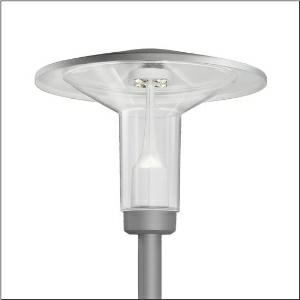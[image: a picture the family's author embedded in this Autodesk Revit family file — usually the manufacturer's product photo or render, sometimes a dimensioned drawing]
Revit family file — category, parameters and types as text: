
# Revit family: laterne_iq___pl1_2s_5xa5255jf14h_d587
name_source: partatom
category: Lighting Fixtures
units: mm (PartAtom-declared; Revit-internal decimal feet)

## family parameters
Cut with Voids When Loaded = No
Host = Face
Light Source = No
Part Type = Normal
Room Calculation Point = No
Round Connector Dimension = Use Diameter
Shared = No

## types (1)
- --- (1 x LED, 2970 lm, 19.3 W, 3000K)
    Apparent Load = 19 VA
    CIE Flux Codes = 25 63 94 98 100
    Color Rendering = 70
    Color Temperature = 3000K
    Default Elevation = 1800 mm
    Description = Lantern iQ, mast luminaire, Module 540 iQ-SR, primary light control with 3 zone facetted reflector, of plastic, silver coated, highly specular, structured, primary optical cover: cover, of PMMA, transparent, light distribution: PL1.2s, light emission: direct distribution, primary light characteristic: symmetric, installation type: post-top, LED, High Power LED, rated luminous flux: 2.970lm, luminous efficacy: 154lm/W, light colour: 730, colour temperature: 3000K, control gear: iQ Street-Remote, control: Auto-Match, Temp-Guard, Lumen-Switch, Night-Set, Smart-Wire, Light-Fading, Desk-Remote (wireless, voltage-free reading and setting of iQ features in the workshop via application-optimized NFC function/RFID function), optimised constant luminous flux control (CLO 2.0), Street-Remote, pre-setting: logarithmic dimming characteristic, with terminal, 6-pole, max. 2.5mm², mains connection: 230..240V, AC, 50/60Hz, start of lifetime: 19W, end of service life: 21W, reduction: 10W, luminaire housing, upper part, of glass-fibre reinforced polyester, coated, Siteco® metallic grey (DB 702S), diameter: 750mm, height: 583mm, spigot size: d x l = 76 x 70mm (post-top) | with reducer (optional accessory) 60 x 70mm, mounting height: 3..5m, post-top mast mounting element, of diecast aluminium, coated, Siteco® metallic grey (DB 702S), Module 540 iQ-SR, traffic white (RAL 9016), equipment: standard, protection rating (complete): IP65, insulation class (complete): insulation class II (safety insulation), certification: CE, ENEC, VDE, packaging unit: 1 piece

Light Distribution: PL1.2s
    Height = 583 mm
    Lamp = 1 x LED
    Lamp Light Flux = 2970 lm
    Lamp Power = 19.3 W
    Lamp count = 1
    Length = 750 mm
    Luminous efficacy = 154 lm/W
    Manufacturer = Siteco
    ModVariant = No
    Model = 5XA5255JF14H
    Number of Poles = 1
    OnlyDefault = Yes
    Power Factor = 1
    Product Name = Laterne iQ | PL1.2s
    Product group = mast luminaire | pylon top
    ProductGroupID = 6100
    Protection Class = Protection class II
    Protection Degree = IP 65
    RLX_Detail_Level = 1
    RLX_Emergency_Light_Flux = 0 lm
    RLX_Emergency_Type = 0
    RLX_Emergency_Type_DB = No
    RlxData = <blob elided: 31601 chars, md5=340e4999>
    Socket = socket
    Standby Power = 0 W
    System Light Flux = 2970 lm
    System Power = 19 W
    Type Comments = factory setting: luminous flux: 100 % | dim-lin: 254 | 403 mA
    Type Image = l_1006050.jpg
    URL = http://relux.com
    VarID = @adj_145922
    Voltage = 0 V
    Weight = 0.00 kg
    Width = 0 mm  [stored 0 ft]

note: [stored X ft] marks values corroborated as IEEE doubles in the binary element streams (Revit-internal decimal feet)

## geometry (parser evidence)
native form markers: Blend x4, Sweep x11
no freeform markers — native parametric forms only
